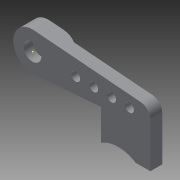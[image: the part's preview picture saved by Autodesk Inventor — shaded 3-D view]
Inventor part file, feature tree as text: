
AUTODESK INVENTOR PART (.ipt)
format: ipt  version: 2015 SP2 (Build 190223200, 223)  size: 172,032 bytes
history: native  units: mm
features: sketch x12, extrude x7, hole x3, fillet x1
ambient origin geometry x8: Origin, YZ Plane, XZ Plane, XY Plane, X Axis, Y Axis, Z Axis, Center Point
bodies: Solid1 (feature_tree)
feature tree (23):
  extrude  "Extrusion1"  Depth=11.314mm
  extrude  "Extrusion2"  Depth=36.0mm
  fillet  "Fillet1"  Radius=7.0mm
  extrude  "Extrusion3"  Depth=4.0mm
  sketch  "Sketch4"  dims[d8=1.5mm d9=0.0mm d10=10.0mm]
  extrude  "Extrusion4"  Depth=10.0mm
  sketch  "Sketch6"  dims[d14=5.8mm d15=5.9mm]
  hole  "Hole1"  [1 undecoded]
  sketch  "Sketch7"  dims[d16=3.0mm d17=0.0mm d18=2.7mm]
  hole  "Hole2"  [1 undecoded]
  extrude  "Extrusion5"  Depth=2.7mm
  extrude  "Extrusion6"  Depth=4.0mm
  hole  "Hole3"  [1 undecoded]
  extrude  "Extrusion7"  Depth=3.0mm
  sketch  "Sketch1"  dims[d0=12.9mm d1=11.314mm]
  sketch  "Sketch2"  dims[d2=5.7mm d3=36.0mm d4=7.0mm]
  sketch  "Sketch3"  dims[d5=4.0mm d6=0.0mm d7=12.9mm]
  sketch  "Sketch5"  dims[d11=11.314mm d12=1.5mm d13=0.0mm]
  sketch  "Sketch8"  dims[d19=2.7mm d20=6.0mm d21=4.0mm d22=2.0mm d23=90.0deg d24=8.0mm d25=20.594885mm d27=6.0mm]
  sketch  "Sketch9"  dims[d28=3.0mm d29=6.0mm]
  sketch  "Sketch10"  dims[d30=3.0mm d31=3.0mm]
  sketch  "Sketch11"  dims[d32=3.0mm]
  sketch  "Sketch12"  dims[d33=3.0mm d34=3.0mm d35=3.0mm d36=6.0mm d37=4.0mm d38=2.0mm d39=90.0deg d40=8.0mm d41=20.594885mm d42=4.0mm d43=0.0mm d44=4.0mm d45=0.0mm d46=15.0mm d47=3.0mm d48=3.0mm d49=3.0mm d50=6.0mm d51=4.0mm d52=2.0mm d53=90.0deg d54=8.0mm d55=20.594885mm d56=4.0mm d57=0.0mm]
note: 3 required parameter values undecoded (feature->parameter linkage not recoverable at this tier; creation-order binding heuristic only, values carry confidence <= 0.55)
